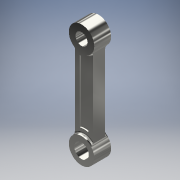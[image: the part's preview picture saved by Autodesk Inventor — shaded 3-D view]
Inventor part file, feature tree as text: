
AUTODESK INVENTOR PART (.ipt)
format: ipt  version: 2018 (Build 220112000, 112)  size: 169,984 bytes
history: native  units: mm
features: extrude x3, sketch x3, projected_geometry x2, mirror x1, fillet x1
ambient origin geometry x8: Origin, YZ Plane, XZ Plane, XY Plane, X Axis, Y Axis, Z Axis, Center Point
bodies: Solid1 (feature_tree)
feature tree (10):
  extrude  "Extrusion1"  Depth=5.0mm
  extrude  "Extrusion2"  Depth=6.0mm
  extrude  "Extrusion3"  Depth=0.75mm TaperAngle=0.0deg
  mirror  "Mirror1"
  fillet  "Fillet1"  Radius=3.75mm
  sketch  "Sketch1"  dims[d0=40.0mm d1=5.0mm]
  sketch  "Sketch2"  dims[d2=10.5mm d3=6.0mm]
  sketch  "Sketch3"  dims[d4=10.5mm d5=7.0mm d6=0.0mm d7=3.75mm d8=5.0mm d9=0.0mm d10=2.0mm d11=0.5mm d12=0.0mm d13=0.75mm]
  projected_geometry  "Projected Loop1"
  projected_geometry  "Project Cut Edges1"
